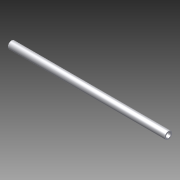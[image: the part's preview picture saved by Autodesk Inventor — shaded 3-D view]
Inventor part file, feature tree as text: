
AUTODESK INVENTOR PART (.ipt)
format: ipt  version: 2011 (Build 150239000, 239)  size: 67,584 bytes
history: native  units: in
note: dims shown in document units (in); Inventor stores cm internally (conversion verified against a paired STEP export)
features: extrude x1, sketch x1
ambient origin geometry x8: Origin, YZ Plane, XZ Plane, XY Plane, X Axis, Y Axis, Z Axis, Center Point
bodies: Solid1 (feature_tree)
feature tree (2):
  extrude  "Extrusion1"  Depth=0.124in
  sketch  "Sketch1"  dims[d0=0.1875in d1=0.124in d2=4.0in d3=0.0in]
